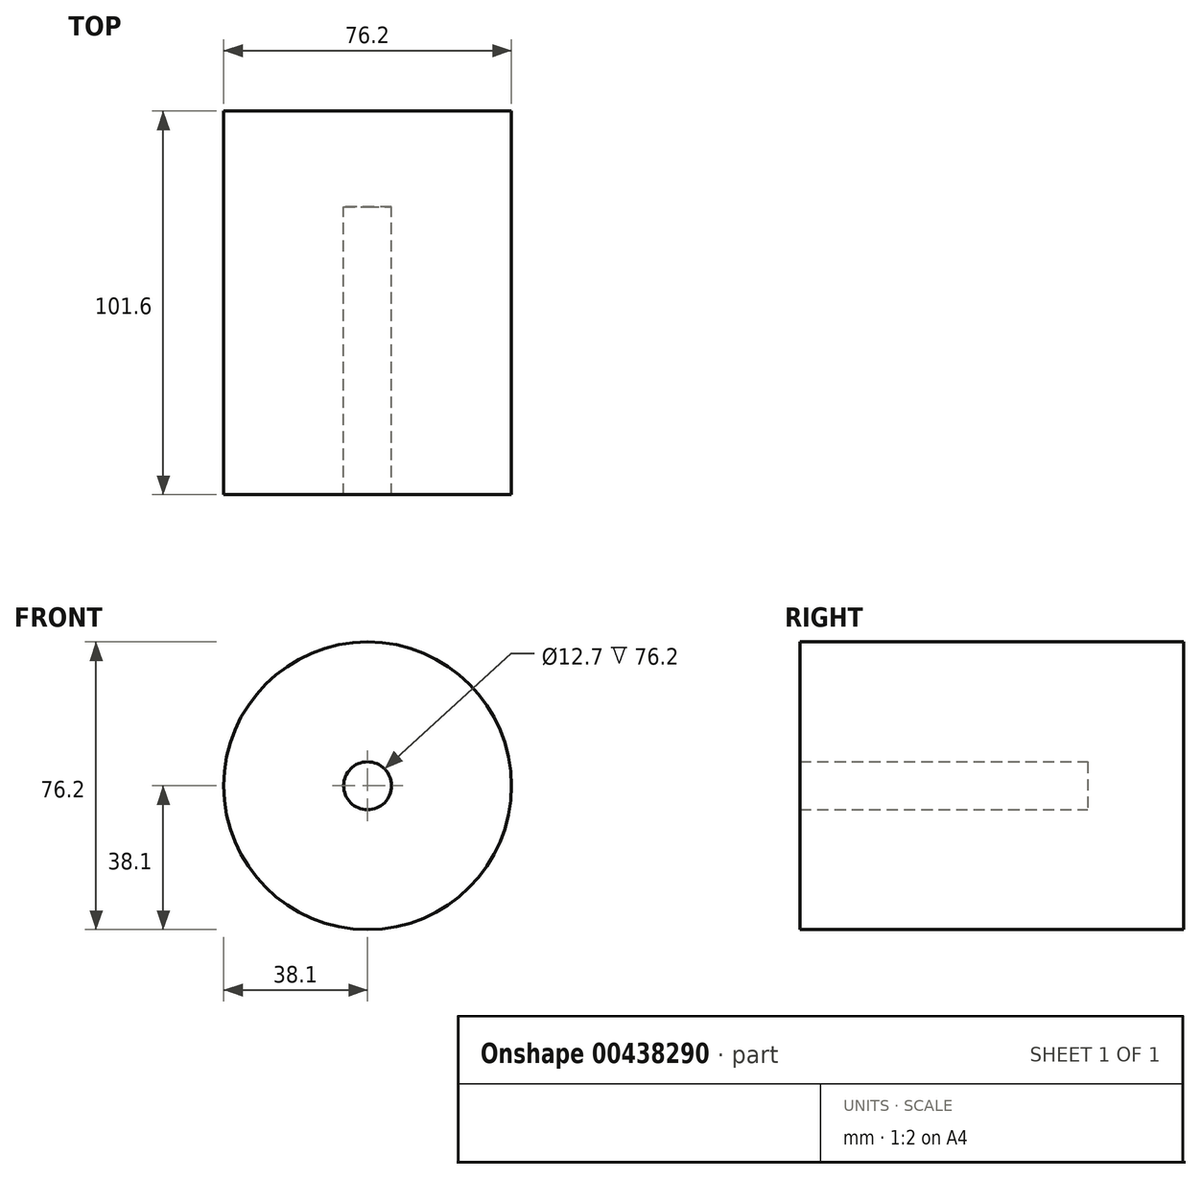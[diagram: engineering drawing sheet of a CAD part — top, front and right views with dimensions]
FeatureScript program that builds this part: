
annotation { "Feature Type Name" : "Feature", "Feature Type Description" : "" }
export const myFeature = defineFeature(function(context is Context, id is Id, definition is map)
    precondition{}
    {
        {
            var Q0;
            Q0=qCreatedBy(makeId("Front.planeOp"),FACE);
            var sketch = newSketch(context, id + "F0", { "sketchPlane" : qUnion([Q0])});
            skCircle(sketch, "E0", {"center": v(0, 0) * mm, "radius": 38.1 * mm});
            skSolve(sketch);
        }
        {
            var Q0;
            Q0=makeQuery(id+"F0.imprint","IMPRINT",FACE,{"disambiguationData":[TD([[makeQuery(id+"F0.imprint","IMPRINT",EDGE,{"derivedFrom":sQuery(id+"F0.wireOp",EDGE,"E0")}),1.0]])]});
            extrude(context, id + "F1", {"entities" : qUnion([Q0]), "depth" : 76.2 * mm, "hasSecondDirection" : true, "secondDirectionOppositeDirection" : true, "secondDirectionDepth" : 25.4 * mm});
        }
        {
            var Q0;
            Q0=qCreatedBy(makeId("Front.planeOp"),FACE);
            var sketch = newSketch(context, id + "F2", { "sketchPlane" : qUnion([Q0])});
            skPoint(sketch, "E1", {"position": v(0, 0) * mm});
            skSolve(sketch);
        }
        {
            var Q0;
            Q0=sQuery(id+"F2.wireOp",VERTEX,"E1");
            var Q1;
            Q1=makeQuery(id+"F1.opExtrude","SWEPT_BODY",BODY,{"disambiguationData":[OSD([sQuery(id+"F0.wireOp",EDGE,"E0")])]});
            hole(context, id + "F3", {"style" : HoleStyle.SIMPLE, "endStyle" : HoleEndStyle.BLIND, "oppositeDirection" : true, "holeDiameter" : 12.7 * mm, "holeDepth" : 101.6 * mm, "isTappedThrough" : true, "tappedDepth" : 12.7 * mm, "tapClearance" : 3, "startFromSketch" : true, "locations" : qUnion([Q0]), "scope" : qUnion([Q1])});
        }
    });
